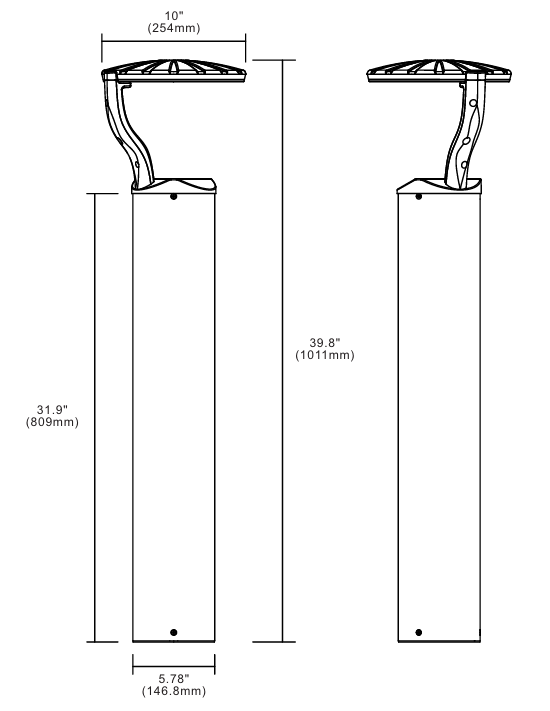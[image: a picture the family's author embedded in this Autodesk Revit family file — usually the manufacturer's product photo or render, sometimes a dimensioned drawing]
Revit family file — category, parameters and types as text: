
# Revit family: Alcon-9035-S-Revit-Family
name_source: partatom
category: Luminarias
units: mm (PartAtom-declared; Revit-internal decimal feet)

## family parameters
Anfitrión = Suelo
Compartido = No
Corte con vacíos al cargar = No
Cota de conector redondo = Usar diámetro
Mantener orientación de anotación = No
Origen de luz = Sí
Punto de cálculo de habitación = No
Siempre vertical = Sí
Tipo de pieza = Normal

## types (1)
- Alcon-9035-S-Revit-Family
    Archivo de red fotométrica = 9035-S(4000K).IES
    Cambio de temperatura de color de luz atenuada = <Ninguno>
    Diámetro de círculo de emisión = 0' - 6 19/32"
    Elevación por defecto = 0' - 0"
    Fabricante = Alcon Lighting
    Filtro de color = 16777215
    Forma visible en renderización = No
    GLASS LENS = Lens
    HOUSING MATERIAL = Housing material
    Modelo = Alcon Lighting 9035-S
    Product page link = https://www.alconlighting.com
    URL = https://www.alconlighting.com
    Ángulo de inclinación = 90.00°

## geometry (parser evidence)
native form markers: Sweep x1
no freeform markers — native parametric forms only
